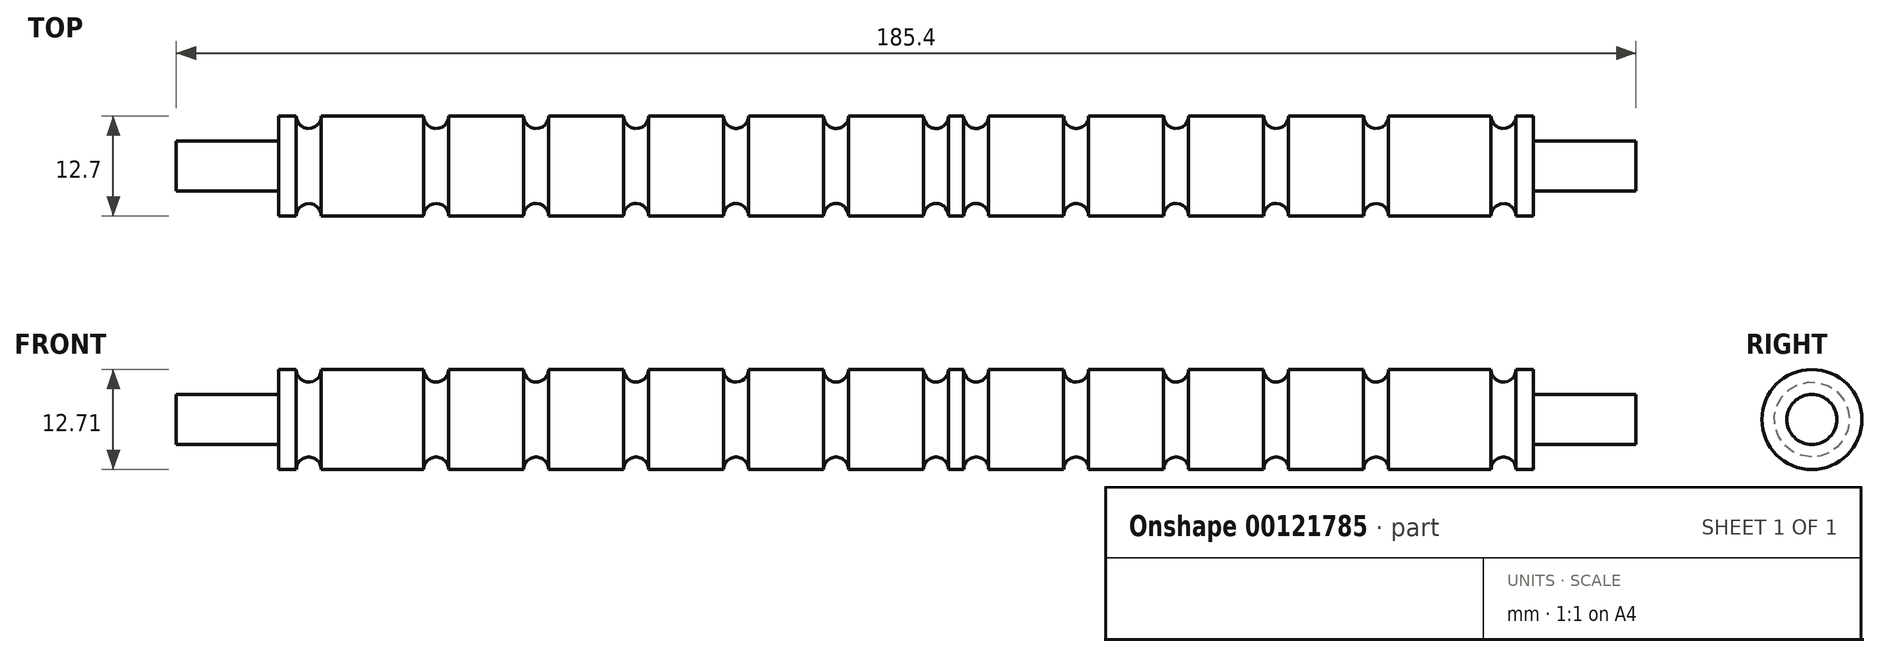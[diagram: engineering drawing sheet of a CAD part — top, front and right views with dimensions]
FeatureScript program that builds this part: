
annotation { "Feature Type Name" : "Feature", "Feature Type Description" : "" }
export const myFeature = defineFeature(function(context is Context, id is Id, definition is map)
    precondition{}
    {
        {
            var Q0;
            Q0=qCreatedBy(makeId("Front.planeOp"),FACE);
            var sketch = newSketch(context, id + "F0", { "sketchPlane" : qUnion([Q0])});
            skLineSegment(sketch, "E0.bottom", {"start": v(79.7, 3.18) * mm, "end": v(77.47, 3.18) * mm});
            skLineSegment(sketch, "E0.top", {"start": v(92.7, -3.17) * mm, "end": v(-92.7, -3.18) * mm});
            skLineSegment(sketch, "E0.left", {"start": v(92.7, 0) * mm, "end": v(92.7, -3.17) * mm});
            skLineSegment(sketch, "E0.right", {"start": v(-92.7, 0) * mm, "end": v(-92.7, -3.17) * mm});
            skPoint(sketch, "E0.middle", {"position": v(0, 0) * mm});
            skLineSegment(sketch, "E1.top", {"start": v(-92.7, 0) * mm, "end": v(-79.7, 0) * mm});
            skLineSegment(sketch, "E1.right", {"start": v(-79.7, 3.18) * mm, "end": v(-79.7, 0) * mm});
            skPoint(sketch, "E2.orphan", {"position": v(-92.7, 3.18) * mm});
            skLineSegment(sketch, "E3", {"start": v(92.7, 0) * mm, "end": v(79.7, 0) * mm});
            skLineSegment(sketch, "E4", {"start": v(79.7, 0) * mm, "end": v(79.7, 3.18) * mm});
            skPoint(sketch, "E5.orphan", {"position": v(92.7, 3.18) * mm});
            skArc(sketch, "E6", {"start": v(-77.47, 3.18) * mm, "mid": v(-75.88, 1.59) * mm, "end": v(-74.3, 3.18) * mm});
            skArc(sketch, "E7", {"start": v(-61.3, 3.18) * mm, "mid": v(-59.7, 1.59) * mm, "end": v(-58.12, 3.18) * mm});
            skArc(sketch, "E8", {"start": v(-48.6, 3.18) * mm, "mid": v(-47, 1.59) * mm, "end": v(-45.42, 3.18) * mm});
            skArc(sketch, "E9", {"start": v(-35.9, 3.18) * mm, "mid": v(-34.3, 1.59) * mm, "end": v(-32.72, 3.18) * mm});
            skArc(sketch, "E10", {"start": v(-23.2, 3.18) * mm, "mid": v(-21.6, 1.59) * mm, "end": v(-20.02, 3.18) * mm});
            skArc(sketch, "E11", {"start": v(-10.5, 3.18) * mm, "mid": v(-8.9, 1.59) * mm, "end": v(-7.32, 3.18) * mm});
            skArc(sketch, "E12", {"start": v(2.2, 3.18) * mm, "mid": v(3.8, 1.59) * mm, "end": v(5.38, 3.18) * mm});
            skLineSegment(sketch, "E13.trimOffspring", {"start": v(2.2, 3.18) * mm, "end": v(-7.32, 3.18) * mm});
            skLineSegment(sketch, "E14.trimOffspring", {"start": v(-10.5, 3.18) * mm, "end": v(-20.02, 3.18) * mm});
            skLineSegment(sketch, "E15.trimOffspring", {"start": v(-23.2, 3.18) * mm, "end": v(-32.72, 3.18) * mm});
            skLineSegment(sketch, "E16.trimOffspring", {"start": v(-35.9, 3.18) * mm, "end": v(-45.42, 3.18) * mm});
            skLineSegment(sketch, "E17.trimOffspring", {"start": v(-48.6, 3.18) * mm, "end": v(-58.12, 3.18) * mm});
            skLineSegment(sketch, "E18.trimOffspring", {"start": v(-61.3, 3.18) * mm, "end": v(-74.3, 3.18) * mm});
            skLineSegment(sketch, "E19.trimOffspring", {"start": v(-77.47, 3.18) * mm, "end": v(-79.7, 3.18) * mm});
            skArc(sketch, "E20.MirrorCS", {"start": v(10.5, 3.18) * mm, "mid": v(8.9, 1.59) * mm, "end": v(7.32, 3.18) * mm});
            skArc(sketch, "E21.MirrorCS", {"start": v(23.2, 3.18) * mm, "mid": v(21.6, 1.59) * mm, "end": v(20.02, 3.18) * mm});
            skArc(sketch, "E22.MirrorCS", {"start": v(35.9, 3.18) * mm, "mid": v(34.3, 1.59) * mm, "end": v(32.72, 3.18) * mm});
            skArc(sketch, "E23.MirrorCS", {"start": v(48.6, 3.18) * mm, "mid": v(47, 1.59) * mm, "end": v(45.42, 3.18) * mm});
            skArc(sketch, "E24.MirrorCS", {"start": v(61.3, 3.18) * mm, "mid": v(59.7, 1.59) * mm, "end": v(58.12, 3.18) * mm});
            skArc(sketch, "E25.MirrorCS", {"start": v(77.47, 3.18) * mm, "mid": v(75.88, 1.59) * mm, "end": v(74.3, 3.18) * mm});
            skLineSegment(sketch, "E26.trimOffspring", {"start": v(7.32, 3.18) * mm, "end": v(5.38, 3.18) * mm});
            skLineSegment(sketch, "E27.trimOffspring", {"start": v(20.02, 3.18) * mm, "end": v(10.5, 3.18) * mm});
            skLineSegment(sketch, "E28.trimOffspring", {"start": v(32.72, 3.18) * mm, "end": v(23.2, 3.18) * mm});
            skLineSegment(sketch, "E29.trimOffspring", {"start": v(45.42, 3.18) * mm, "end": v(35.9, 3.18) * mm});
            skLineSegment(sketch, "E30.trimOffspring", {"start": v(58.12, 3.18) * mm, "end": v(48.6, 3.18) * mm});
            skLineSegment(sketch, "E31.trimOffspring", {"start": v(74.3, 3.18) * mm, "end": v(61.3, 3.18) * mm});
            skSolve(sketch);
        }
        {
            var Q0;
            Q0 = qSketchRegion(id + "F0", true);
            var Q1;
            Q1=sQuery(id+"F0.wireOp",EDGE,"E0.top");
            revolve(context, id + "F1", {"entities" : qUnion([Q0]), "axis" : qUnion([Q1]), "revolveType" : RevolveType.FULL});
        }
    });
